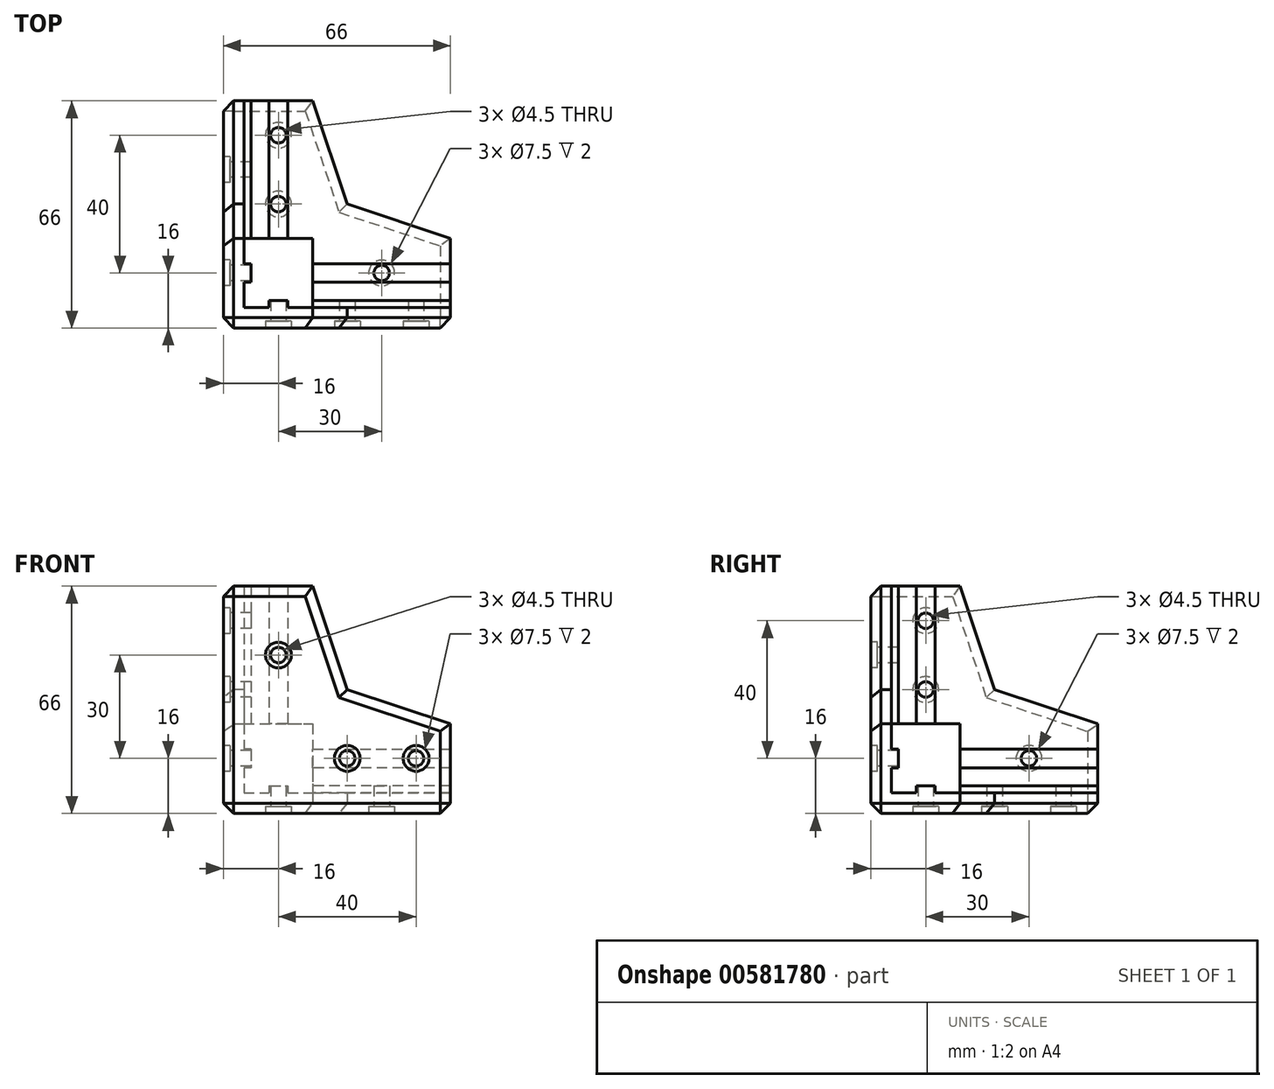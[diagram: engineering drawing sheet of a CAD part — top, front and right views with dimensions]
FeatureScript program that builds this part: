
annotation { "Feature Type Name" : "Feature", "Feature Type Description" : "" }
export const myFeature = defineFeature(function(context is Context, id is Id, definition is map)
    precondition{}
    {
        {
            var Q0;
            Q0=qCreatedBy(makeId("Top.planeOp"),FACE);
            var sketch = newSketch(context, id + "F0", { "sketchPlane" : qUnion([Q0])});
            skLineSegment(sketch, "E0", {"start": v(0, 0) * mm, "end": v(0, 66) * mm});
            skLineSegment(sketch, "E1", {"start": v(0, 66) * mm, "end": v(26, 66) * mm});
            skLineSegment(sketch, "E2", {"start": v(26, 66) * mm, "end": v(26, 26) * mm});
            skLineSegment(sketch, "E3", {"start": v(26, 26) * mm, "end": v(66, 26) * mm});
            skLineSegment(sketch, "E4", {"start": v(66, 26) * mm, "end": v(66, 0) * mm});
            skLineSegment(sketch, "E5", {"start": v(66, 0) * mm, "end": v(0, 0) * mm});
            skLineSegment(sketch, "E6", {"start": v(66, 6) * mm, "end": v(6, 6) * mm, "construction": true});
            skLineSegment(sketch, "E7", {"start": v(6, 6) * mm, "end": v(6, 66) * mm, "construction": true});
            skSolve(sketch);
        }
        {
            var Q0;
            Q0=qSketchRegion(id+"F0",true);
            extrude(context, id + "F1", {"entities" : qUnion([Q0]), "depth" : 6 * mm});
        }
        {
            var Q0;
            Q0=makeQuery(id+"F1.opExtrude","CAP_FACE",FACE,{"disambiguationData":[OSD([sQuery(id+"F0.wireOp",EDGE,"E0"),sQuery(id+"F0.wireOp",EDGE,"E1"),sQuery(id+"F0.wireOp",EDGE,"E2"),sQuery(id+"F0.wireOp",EDGE,"E3"),sQuery(id+"F0.wireOp",EDGE,"E4"),sQuery(id+"F0.wireOp",EDGE,"E5")])],"isStart":false});
            var sketch = newSketch(context, id + "F2", { "sketchPlane" : qUnion([Q0])});
            skLineSegment(sketch, "E8", {"start": v(0, 66) * mm, "end": v(6, 66) * mm});
            skLineSegment(sketch, "E9", {"start": v(6, 66) * mm, "end": v(6, 6) * mm});
            skLineSegment(sketch, "E10", {"start": v(6, 6) * mm, "end": v(66, 6) * mm});
            skLineSegment(sketch, "E11", {"start": v(66, 6) * mm, "end": v(66, 0) * mm});
            skLineSegment(sketch, "E12", {"start": v(66, 0) * mm, "end": v(0, 0) * mm});
            skLineSegment(sketch, "E13", {"start": v(0, 0) * mm, "end": v(0, 66) * mm});
            skSolve(sketch);
        }
        {
            var Q0;
            Q0=makeQuery(id+"F2.imprint","IMPRINT",FACE,{"disambiguationData":[TD([[makeQuery(id+"F2.imprint","IMPRINT",EDGE,{"derivedFrom":sQuery(id+"F2.wireOp",EDGE,"E8")}),-1.0]])]});
            extrude(context, id + "F3", {"entities" : qUnion([Q0]), "operationType" : NewBodyOperationType.ADD, "depth" : 20 * mm});
        }
        {
            var Q0;
            Q0=makeQuery(id+"F3.opExtrude","CAP_FACE",FACE,{"disambiguationData":[OSD([sQuery(id+"F2.wireOp",EDGE,"E8"),sQuery(id+"F2.wireOp",EDGE,"E9"),sQuery(id+"F2.wireOp",EDGE,"E10"),sQuery(id+"F2.wireOp",EDGE,"E11"),sQuery(id+"F2.wireOp",EDGE,"E12"),sQuery(id+"F2.wireOp",EDGE,"E13")])],"isStart":false});
            var sketch = newSketch(context, id + "F4", { "sketchPlane" : qUnion([Q0])});
            skLineSegment(sketch, "E14", {"start": v(6, 26) * mm, "end": v(0, 26) * mm});
            skLineSegment(sketch, "E15", {"start": v(0, 26) * mm, "end": v(0, 0) * mm});
            skLineSegment(sketch, "E16", {"start": v(0, 0) * mm, "end": v(26, 0) * mm});
            skLineSegment(sketch, "E17", {"start": v(26, 0) * mm, "end": v(26, 6) * mm});
            skLineSegment(sketch, "E18", {"start": v(26, 6) * mm, "end": v(6, 6) * mm});
            skLineSegment(sketch, "E19", {"start": v(6, 6) * mm, "end": v(6, 26) * mm});
            skSolve(sketch);
        }
        {
            var Q0;
            Q0=qSketchRegion(id+"F4",true);
            extrude(context, id + "F5", {"entities" : qUnion([Q0]), "operationType" : NewBodyOperationType.ADD, "depth" : 40 * mm});
        }
        {
            var Q0;
            Q0=makeQuery(id+"F1.opExtrude","CAP_FACE",FACE,{"disambiguationData":[OSD([sQuery(id+"F0.wireOp",EDGE,"E0"),sQuery(id+"F0.wireOp",EDGE,"E1"),sQuery(id+"F0.wireOp",EDGE,"E2"),sQuery(id+"F0.wireOp",EDGE,"E3"),sQuery(id+"F0.wireOp",EDGE,"E4"),sQuery(id+"F0.wireOp",EDGE,"E5")])],"isStart":false});
            var sketch = newSketch(context, id + "F6", { "sketchPlane" : qUnion([Q0])});
            skLineSegment(sketch, "E20", {"start": v(66, 16) * mm, "end": v(6, 16) * mm, "construction": true});
            skLineSegment(sketch, "E21", {"start": v(16, 66) * mm, "end": v(16, 6) * mm, "construction": true});
            skLineSegment(sketch, "E22", {"start": v(16, 6) * mm, "end": v(18.71, 6) * mm});
            skLineSegment(sketch, "E23", {"start": v(18.71, 6) * mm, "end": v(18.71, 8) * mm});
            skLineSegment(sketch, "E24", {"start": v(18.71, 8) * mm, "end": v(13.3, 8) * mm});
            skLineSegment(sketch, "E25", {"start": v(13.3, 8) * mm, "end": v(13.3, 6) * mm});
            skLineSegment(sketch, "E26", {"start": v(13.3, 6) * mm, "end": v(16, 6) * mm});
            skLineSegment(sketch, "E27", {"start": v(6, 16) * mm, "end": v(6, 18.7) * mm});
            skLineSegment(sketch, "E28", {"start": v(6, 18.7) * mm, "end": v(8, 18.7) * mm});
            skLineSegment(sketch, "E29", {"start": v(8, 18.7) * mm, "end": v(8, 13.29) * mm});
            skLineSegment(sketch, "E30", {"start": v(8, 13.29) * mm, "end": v(6, 13.29) * mm});
            skLineSegment(sketch, "E31", {"start": v(6, 13.29) * mm, "end": v(6, 16) * mm});
            skSolve(sketch);
        }
        {
            var Q0;
            Q0=qSketchRegion(id+"F6",true);
            extrude(context, id + "F7", {"entities" : qUnion([Q0]), "operationType" : NewBodyOperationType.ADD, "depth" : 60 * mm});
        }
        {
            var Q0;
            Q0=makeQuery(id+"F1.opExtrude","CAP_FACE",FACE,{"disambiguationData":[OSD([sQuery(id+"F0.wireOp",EDGE,"E0"),sQuery(id+"F0.wireOp",EDGE,"E1"),sQuery(id+"F0.wireOp",EDGE,"E2"),sQuery(id+"F0.wireOp",EDGE,"E3"),sQuery(id+"F0.wireOp",EDGE,"E4"),sQuery(id+"F0.wireOp",EDGE,"E5")])],"isStart":false});
            var sketch = newSketch(context, id + "F8", { "sketchPlane" : qUnion([Q0])});
            skLineSegment(sketch, "E32", {"start": v(66, 16) * mm, "end": v(8, 16) * mm, "construction": true});
            skLineSegment(sketch, "E33", {"start": v(66, 16) * mm, "end": v(66, 18.7) * mm});
            skLineSegment(sketch, "E34", {"start": v(66, 18.7) * mm, "end": v(26, 18.7) * mm});
            skLineSegment(sketch, "E35", {"start": v(26, 18.7) * mm, "end": v(26, 13.29) * mm});
            skLineSegment(sketch, "E36", {"start": v(26, 13.29) * mm, "end": v(66, 13.29) * mm});
            skLineSegment(sketch, "E37", {"start": v(66, 13.29) * mm, "end": v(66, 16) * mm});
            skLineSegment(sketch, "E38", {"start": v(16, 66) * mm, "end": v(16, 8) * mm, "construction": true});
            skLineSegment(sketch, "E39", {"start": v(16, 66) * mm, "end": v(13.3, 66) * mm});
            skLineSegment(sketch, "E40", {"start": v(13.3, 66) * mm, "end": v(13.3, 26) * mm});
            skLineSegment(sketch, "E41", {"start": v(13.3, 26) * mm, "end": v(18.7, 26) * mm});
            skLineSegment(sketch, "E42", {"start": v(18.7, 26) * mm, "end": v(18.7, 66) * mm});
            skLineSegment(sketch, "E43", {"start": v(18.7, 66) * mm, "end": v(16, 66) * mm});
            skSolve(sketch);
        }
        {
            var Q0;
            Q0=qSketchRegion(id+"F8",true);
            extrude(context, id + "F9", {"entities" : qUnion([Q0]), "operationType" : NewBodyOperationType.ADD, "depth" : 2 * mm});
        }
        {
            var Q0;
            {var subQ1=sQuery(id+"F2.wireOp",EDGE,"E10");var subQ2=sQuery(id+"F0.wireOp",EDGE,"E4");var subQ3=sQuery(id+"F4.wireOp",EDGE,"E18");Q0=makeQuery(id+"F7.boolean.opBoolean","SPLIT",FACE,{"disambiguationData":[TD([makeQuery(id+"F1.opExtrude","SWEPT_FACE",FACE,{"disambiguationData":[OSD([subQ2])]})])],"derivedFrom":makeQuery(id+"F5.boolean.opBoolean","MERGE",FACE,{"derivedFrom":[makeQuery(id+"F3.opExtrude","SWEPT_FACE",FACE,{"disambiguationData":[OSD([subQ1])]}),makeQuery(id+"F5.opExtrude","SWEPT_FACE",FACE,{"disambiguationData":[OSD([subQ3])]})]})});}
            var sketch = newSketch(context, id + "F10", { "sketchPlane" : qUnion([Q0])});
            skLineSegment(sketch, "E44", {"start": v(-66, 16) * mm, "end": v(-26, 16) * mm, "construction": true});
            skLineSegment(sketch, "E45", {"start": v(-66, 16) * mm, "end": v(-66, 13.3) * mm});
            skLineSegment(sketch, "E46", {"start": v(-66, 13.3) * mm, "end": v(-26, 13.3) * mm});
            skLineSegment(sketch, "E47", {"start": v(-26, 13.3) * mm, "end": v(-26, 16) * mm});
            skLineSegment(sketch, "E48", {"start": v(-26, 18.71) * mm, "end": v(-66, 18.71) * mm});
            skLineSegment(sketch, "E49", {"start": v(-66, 18.71) * mm, "end": v(-66, 16) * mm});
            skLineSegment(sketch, "E50", {"start": v(-26, 18.71) * mm, "end": v(-26, 16) * mm});
            skSolve(sketch);
        }
        {
            var Q0;
            Q0=qSketchRegion(id+"F10",true);
            extrude(context, id + "F11", {"entities" : qUnion([Q0]), "operationType" : NewBodyOperationType.ADD, "depth" : 2 * mm});
        }
        {
            var Q0;
            {var subQ0=sQuery(id+"F2.wireOp",EDGE,"E9");var subQ3=sQuery(id+"F0.wireOp",EDGE,"E1");var subQ5=sQuery(id+"F4.wireOp",EDGE,"E19");Q0=makeQuery(id+"F7.boolean.opBoolean","SPLIT",FACE,{"disambiguationData":[TD([makeQuery(id+"F1.opExtrude","SWEPT_FACE",FACE,{"disambiguationData":[OSD([subQ3])]})])],"derivedFrom":makeQuery(id+"F5.boolean.opBoolean","MERGE",FACE,{"derivedFrom":[makeQuery(id+"F3.opExtrude","SWEPT_FACE",FACE,{"disambiguationData":[OSD([subQ0])]}),makeQuery(id+"F5.opExtrude","SWEPT_FACE",FACE,{"disambiguationData":[OSD([subQ5])]})]})});}
            var sketch = newSketch(context, id + "F12", { "sketchPlane" : qUnion([Q0])});
            skLineSegment(sketch, "E51", {"start": v(66, 16) * mm, "end": v(26, 16) * mm, "construction": true});
            skLineSegment(sketch, "E52", {"start": v(66, 16) * mm, "end": v(66, 18.71) * mm});
            skLineSegment(sketch, "E53", {"start": v(66, 18.71) * mm, "end": v(26, 18.7) * mm});
            skLineSegment(sketch, "E54", {"start": v(26, 18.7) * mm, "end": v(26, 13.29) * mm});
            skLineSegment(sketch, "E55", {"start": v(26, 13.29) * mm, "end": v(66, 13.29) * mm});
            skLineSegment(sketch, "E56", {"start": v(66, 16) * mm, "end": v(66, 13.29) * mm});
            skSolve(sketch);
        }
        {
            var Q0;
            Q0=qSketchRegion(id+"F12",true);
            extrude(context, id + "F13", {"entities" : qUnion([Q0]), "operationType" : NewBodyOperationType.ADD, "depth" : 2 * mm});
        }
        {
            var Q0;
            Q0=makeQuery(id+"F5.boolean.opBoolean","MERGE",FACE,{"derivedFrom":[makeQuery(id+"F3.boolean.opBoolean","MERGE",FACE,{"derivedFrom":[makeQuery(id+"F1.opExtrude","SWEPT_FACE",FACE,{"disambiguationData":[OSD([sQuery(id+"F0.wireOp",EDGE,"E5")])]}),makeQuery(id+"F3.opExtrude","SWEPT_FACE",FACE,{"disambiguationData":[OSD([sQuery(id+"F2.wireOp",EDGE,"E12")])]})]}),makeQuery(id+"F5.opExtrude","SWEPT_FACE",FACE,{"disambiguationData":[OSD([sQuery(id+"F4.wireOp",EDGE,"E16")])]})]});
            var sketch = newSketch(context, id + "F14", { "sketchPlane" : qUnion([Q0])});
            skLineSegment(sketch, "E57", {"start": v(6, 66) * mm, "end": v(6, 6) * mm, "construction": true});
            skLineSegment(sketch, "E58", {"start": v(6, 6) * mm, "end": v(66, 6) * mm, "construction": true});
            skCircle(sketch, "E59", {"center": v(56, 16) * mm, "radius": 2.25 * mm});
            skCircle(sketch, "E60", {"center": v(36, 16) * mm, "radius": 2.25 * mm});
            skCircle(sketch, "E61", {"center": v(16, 46) * mm, "radius": 2.25 * mm});
            skLineSegment(sketch, "E62", {"start": v(26, 26) * mm, "end": v(6, 26) * mm, "construction": true});
            skLineSegment(sketch, "E63", {"start": v(26, 26) * mm, "end": v(26, 6) * mm, "construction": true});
            skSolve(sketch);
        }
        {
            var Q0;
            Q0=makeQuery(id+"F14.imprint","IMPRINT",FACE,{"disambiguationData":[TD([[makeQuery(id+"F14.imprint","IMPRINT",EDGE,{"derivedFrom":sQuery(id+"F14.wireOp",EDGE,"E59")}),1.0]])]});
            var Q1;
            Q1=makeQuery(id+"F14.imprint","IMPRINT",FACE,{"disambiguationData":[TD([[makeQuery(id+"F14.imprint","IMPRINT",EDGE,{"derivedFrom":sQuery(id+"F14.wireOp",EDGE,"E61")}),1.0]])]});
            var Q2;
            Q2=makeQuery(id+"F14.imprint","IMPRINT",FACE,{"disambiguationData":[TD([[makeQuery(id+"F14.imprint","IMPRINT",EDGE,{"derivedFrom":sQuery(id+"F14.wireOp",EDGE,"E60")}),1.0]])]});
            extrude(context, id + "F15", {"entities" : qUnion([Q0, Q1, Q2]), "operationType" : NewBodyOperationType.REMOVE, "endBound" : BoundingType.UP_TO_NEXT, "oppositeDirection" : true, "depth" : 25 * mm});
        }
        {
            var Q0;
            Q0=makeQuery(id+"F5.boolean.opBoolean","MERGE",FACE,{"derivedFrom":[makeQuery(id+"F3.boolean.opBoolean","MERGE",FACE,{"derivedFrom":[makeQuery(id+"F1.opExtrude","SWEPT_FACE",FACE,{"disambiguationData":[OSD([sQuery(id+"F0.wireOp",EDGE,"E0")])]}),makeQuery(id+"F3.opExtrude","SWEPT_FACE",FACE,{"disambiguationData":[OSD([sQuery(id+"F2.wireOp",EDGE,"E13")])]})]}),makeQuery(id+"F5.opExtrude","SWEPT_FACE",FACE,{"disambiguationData":[OSD([sQuery(id+"F4.wireOp",EDGE,"E15")])]})]});
            var sketch = newSketch(context, id + "F16", { "sketchPlane" : qUnion([Q0])});
            skLineSegment(sketch, "E64", {"start": v(-6, 66) * mm, "end": v(-6, 6) * mm, "construction": true});
            skLineSegment(sketch, "E65", {"start": v(-6, 6) * mm, "end": v(-66, 6) * mm, "construction": true});
            skCircle(sketch, "E66", {"center": v(-16, 56) * mm, "radius": 2.25 * mm});
            skCircle(sketch, "E67", {"center": v(-46, 16) * mm, "radius": 2.25 * mm});
            skCircle(sketch, "E68", {"center": v(-16, 36) * mm, "radius": 2.25 * mm});
            skSolve(sketch);
        }
        {
            var Q0;
            Q0=qSketchRegion(id+"F16",true);
            extrude(context, id + "F17", {"entities" : qUnion([Q0]), "operationType" : NewBodyOperationType.REMOVE, "endBound" : BoundingType.UP_TO_NEXT, "oppositeDirection" : true, "depth" : 25 * mm});
        }
        {
            var Q0;
            Q0=makeQuery(id+"F1.opExtrude","CAP_FACE",FACE,{"disambiguationData":[OSD([sQuery(id+"F0.wireOp",EDGE,"E0"),sQuery(id+"F0.wireOp",EDGE,"E1"),sQuery(id+"F0.wireOp",EDGE,"E2"),sQuery(id+"F0.wireOp",EDGE,"E3"),sQuery(id+"F0.wireOp",EDGE,"E4"),sQuery(id+"F0.wireOp",EDGE,"E5")])],"isStart":true});
            var sketch = newSketch(context, id + "F18", { "sketchPlane" : qUnion([Q0])});
            skLineSegment(sketch, "E69", {"start": v(66, -6) * mm, "end": v(6, -6) * mm, "construction": true});
            skLineSegment(sketch, "E70", {"start": v(6, -6) * mm, "end": v(6, -66) * mm, "construction": true});
            skCircle(sketch, "E71", {"center": v(46, -16) * mm, "radius": 2.25 * mm});
            skCircle(sketch, "E72", {"center": v(16, -56) * mm, "radius": 2.25 * mm});
            skCircle(sketch, "E73", {"center": v(16, -36) * mm, "radius": 2.25 * mm});
            skSolve(sketch);
        }
        {
            var Q0;
            Q0=qSketchRegion(id+"F18",true);
            extrude(context, id + "F19", {"entities" : qUnion([Q0]), "operationType" : NewBodyOperationType.REMOVE, "endBound" : BoundingType.UP_TO_NEXT, "oppositeDirection" : true, "depth" : 25 * mm});
        }
        {
            var Q0;
            Q0=makeQuery(id+"F5.boolean.opBoolean","MERGE",FACE,{"derivedFrom":[makeQuery(id+"F3.boolean.opBoolean","MERGE",FACE,{"derivedFrom":[makeQuery(id+"F1.opExtrude","SWEPT_FACE",FACE,{"disambiguationData":[OSD([sQuery(id+"F0.wireOp",EDGE,"E5")])]}),makeQuery(id+"F3.opExtrude","SWEPT_FACE",FACE,{"disambiguationData":[OSD([sQuery(id+"F2.wireOp",EDGE,"E12")])]})]}),makeQuery(id+"F5.opExtrude","SWEPT_FACE",FACE,{"disambiguationData":[OSD([sQuery(id+"F4.wireOp",EDGE,"E16")])]})]});
            var sketch = newSketch(context, id + "F20", { "sketchPlane" : qUnion([Q0])});
            skCircle(sketch, "E74", {"center": v(16, 46) * mm, "radius": 3.75 * mm});
            skCircle(sketch, "E75", {"center": v(36, 16) * mm, "radius": 3.75 * mm});
            skCircle(sketch, "E76", {"center": v(56, 16) * mm, "radius": 3.75 * mm});
            skSolve(sketch);
        }
        {
            var Q0;
            Q0=qSketchRegion(id+"F20",true);
            extrude(context, id + "F21", {"entities" : qUnion([Q0]), "operationType" : NewBodyOperationType.REMOVE, "oppositeDirection" : true, "depth" : 2 * mm});
        }
        {
            var Q0;
            Q0=makeQuery(id+"F5.boolean.opBoolean","MERGE",FACE,{"derivedFrom":[makeQuery(id+"F3.boolean.opBoolean","MERGE",FACE,{"derivedFrom":[makeQuery(id+"F1.opExtrude","SWEPT_FACE",FACE,{"disambiguationData":[OSD([sQuery(id+"F0.wireOp",EDGE,"E0")])]}),makeQuery(id+"F3.opExtrude","SWEPT_FACE",FACE,{"disambiguationData":[OSD([sQuery(id+"F2.wireOp",EDGE,"E13")])]})]}),makeQuery(id+"F5.opExtrude","SWEPT_FACE",FACE,{"disambiguationData":[OSD([sQuery(id+"F4.wireOp",EDGE,"E15")])]})]});
            var sketch = newSketch(context, id + "F22", { "sketchPlane" : qUnion([Q0])});
            skCircle(sketch, "E77", {"center": v(-16, 56) * mm, "radius": 3.75 * mm});
            skCircle(sketch, "E78", {"center": v(-46, 16) * mm, "radius": 3.75 * mm});
            skCircle(sketch, "E79", {"center": v(-16, 36) * mm, "radius": 3.75 * mm});
            skSolve(sketch);
        }
        {
            var Q0;
            Q0=qSketchRegion(id+"F22",true);
            extrude(context, id + "F23", {"entities" : qUnion([Q0]), "operationType" : NewBodyOperationType.REMOVE, "oppositeDirection" : true, "depth" : 2 * mm});
        }
        {
            var Q0;
            Q0=makeQuery(id+"F1.opExtrude","CAP_FACE",FACE,{"disambiguationData":[OSD([sQuery(id+"F0.wireOp",EDGE,"E0"),sQuery(id+"F0.wireOp",EDGE,"E1"),sQuery(id+"F0.wireOp",EDGE,"E2"),sQuery(id+"F0.wireOp",EDGE,"E3"),sQuery(id+"F0.wireOp",EDGE,"E4"),sQuery(id+"F0.wireOp",EDGE,"E5")])],"isStart":true});
            var sketch = newSketch(context, id + "F24", { "sketchPlane" : qUnion([Q0])});
            skCircle(sketch, "E80", {"center": v(16, -56) * mm, "radius": 3.75 * mm});
            skCircle(sketch, "E81", {"center": v(46, -16) * mm, "radius": 3.75 * mm});
            skCircle(sketch, "E82", {"center": v(16, -36) * mm, "radius": 3.75 * mm});
            skSolve(sketch);
        }
        {
            var Q0;
            Q0=qSketchRegion(id+"F24",true);
            extrude(context, id + "F25", {"entities" : qUnion([Q0]), "operationType" : NewBodyOperationType.REMOVE, "oppositeDirection" : true, "depth" : 2 * mm});
        }
        {
            var Q0;
            Q0=makeQuery(id+"F1.opExtrude","CAP_FACE",FACE,{"disambiguationData":[OSD([sQuery(id+"F0.wireOp",EDGE,"E0"),sQuery(id+"F0.wireOp",EDGE,"E1"),sQuery(id+"F0.wireOp",EDGE,"E2"),sQuery(id+"F0.wireOp",EDGE,"E3"),sQuery(id+"F0.wireOp",EDGE,"E4"),sQuery(id+"F0.wireOp",EDGE,"E5")])],"isStart":false});
            var sketch = newSketch(context, id + "F26", { "sketchPlane" : qUnion([Q0])});
            skLineSegment(sketch, "E83.bottom", {"start": v(6, 6) * mm, "end": v(26, 6) * mm});
            skLineSegment(sketch, "E83.top", {"start": v(6, 26) * mm, "end": v(26, 26) * mm});
            skLineSegment(sketch, "E83.left", {"start": v(6, 6) * mm, "end": v(6, 26) * mm});
            skLineSegment(sketch, "E83.right", {"start": v(26, 6) * mm, "end": v(26, 26) * mm});
            skSolve(sketch);
        }
        {
            var Q0;
            Q0=qSketchRegion(id+"F26",true);
            extrude(context, id + "F27", {"entities" : qUnion([Q0]), "operationType" : NewBodyOperationType.ADD, "depth" : 20 * mm});
        }
        {
            var Q0;
            Q0=makeQuery(id+"F5.boolean.opBoolean","MERGE",FACE,{"derivedFrom":[makeQuery(id+"F3.boolean.opBoolean","MERGE",FACE,{"derivedFrom":[makeQuery(id+"F1.opExtrude","SWEPT_FACE",FACE,{"disambiguationData":[OSD([sQuery(id+"F0.wireOp",EDGE,"E5")])]}),makeQuery(id+"F3.opExtrude","SWEPT_FACE",FACE,{"disambiguationData":[OSD([sQuery(id+"F2.wireOp",EDGE,"E12")])]})]}),makeQuery(id+"F5.opExtrude","SWEPT_FACE",FACE,{"disambiguationData":[OSD([sQuery(id+"F4.wireOp",EDGE,"E16")])]})]});
            var sketch = newSketch(context, id + "F28", { "sketchPlane" : qUnion([Q0])});
            skLineSegment(sketch, "E84", {"start": v(26, 36) * mm, "end": v(36, 36) * mm, "construction": true});
            skLineSegment(sketch, "E85", {"start": v(36, 36) * mm, "end": v(36, 26) * mm, "construction": true});
            skLineSegment(sketch, "E86", {"start": v(26, 66) * mm, "end": v(36, 36) * mm});
            skLineSegment(sketch, "E87", {"start": v(36, 36) * mm, "end": v(66, 26) * mm});
            skLineSegment(sketch, "E88", {"start": v(66, 26) * mm, "end": v(26, 26) * mm});
            skLineSegment(sketch, "E89", {"start": v(26, 26) * mm, "end": v(26, 66) * mm});
            skSolve(sketch);
        }
        {
            var Q0;
            Q0=qSketchRegion(id+"F28",true);
            extrude(context, id + "F29", {"entities" : qUnion([Q0]), "operationType" : NewBodyOperationType.ADD, "oppositeDirection" : true, "depth" : 6 * mm});
        }
        {
            var Q0;
            Q0=makeQuery(id+"F5.boolean.opBoolean","MERGE",FACE,{"derivedFrom":[makeQuery(id+"F3.boolean.opBoolean","MERGE",FACE,{"derivedFrom":[makeQuery(id+"F1.opExtrude","SWEPT_FACE",FACE,{"disambiguationData":[OSD([sQuery(id+"F0.wireOp",EDGE,"E0")])]}),makeQuery(id+"F3.opExtrude","SWEPT_FACE",FACE,{"disambiguationData":[OSD([sQuery(id+"F2.wireOp",EDGE,"E13")])]})]}),makeQuery(id+"F5.opExtrude","SWEPT_FACE",FACE,{"disambiguationData":[OSD([sQuery(id+"F4.wireOp",EDGE,"E15")])]})]});
            var sketch = newSketch(context, id + "F30", { "sketchPlane" : qUnion([Q0])});
            skLineSegment(sketch, "E90", {"start": v(-26, 36) * mm, "end": v(-36, 36) * mm, "construction": true});
            skLineSegment(sketch, "E91", {"start": v(-36, 36) * mm, "end": v(-36, 26) * mm, "construction": true});
            skLineSegment(sketch, "E92", {"start": v(-26, 66) * mm, "end": v(-36, 36) * mm});
            skLineSegment(sketch, "E93", {"start": v(-36, 36) * mm, "end": v(-66, 26) * mm});
            skLineSegment(sketch, "E94", {"start": v(-66, 26) * mm, "end": v(-26, 26) * mm});
            skLineSegment(sketch, "E95", {"start": v(-26, 26) * mm, "end": v(-26, 66) * mm});
            skSolve(sketch);
        }
        {
            var Q0;
            Q0=qSketchRegion(id+"F30",true);
            extrude(context, id + "F31", {"entities" : qUnion([Q0]), "operationType" : NewBodyOperationType.ADD, "oppositeDirection" : true, "depth" : 6 * mm});
        }
        {
            var Q0;
            Q0=makeQuery(id+"F1.opExtrude","CAP_FACE",FACE,{"disambiguationData":[OSD([sQuery(id+"F0.wireOp",EDGE,"E0"),sQuery(id+"F0.wireOp",EDGE,"E1"),sQuery(id+"F0.wireOp",EDGE,"E2"),sQuery(id+"F0.wireOp",EDGE,"E3"),sQuery(id+"F0.wireOp",EDGE,"E4"),sQuery(id+"F0.wireOp",EDGE,"E5")])],"isStart":true});
            var sketch = newSketch(context, id + "F32", { "sketchPlane" : qUnion([Q0])});
            skLineSegment(sketch, "E96", {"start": v(36, -26) * mm, "end": v(36, -36) * mm, "construction": true});
            skLineSegment(sketch, "E97", {"start": v(36, -36) * mm, "end": v(26, -36) * mm, "construction": true});
            skLineSegment(sketch, "E98", {"start": v(66, -26) * mm, "end": v(36, -36) * mm});
            skLineSegment(sketch, "E99", {"start": v(36, -36) * mm, "end": v(26, -66) * mm});
            skLineSegment(sketch, "E100", {"start": v(26, -66) * mm, "end": v(26, -26) * mm});
            skLineSegment(sketch, "E101", {"start": v(26, -26) * mm, "end": v(66, -26) * mm});
            skSolve(sketch);
        }
        {
            var Q0;
            Q0=qSketchRegion(id+"F32",true);
            extrude(context, id + "F33", {"entities" : qUnion([Q0]), "operationType" : NewBodyOperationType.ADD, "oppositeDirection" : true, "depth" : 6 * mm});
        }
        {
            var Q0;
            Q0=makeQuery(id+"F1.opExtrude","CAP_EDGE",EDGE,{"disambiguationData":[OSD([sQuery(id+"F0.wireOp",EDGE,"E5")])],"isStart":true});
            var Q1;
            Q1=makeQuery(id+"F1.opExtrude","CAP_EDGE",EDGE,{"disambiguationData":[OSD([sQuery(id+"F0.wireOp",EDGE,"E4")])],"isStart":true});
            var Q2;
            Q2=makeQuery(id+"F33.opExtrude","CAP_EDGE",EDGE,{"disambiguationData":[OSD([sQuery(id+"F32.wireOp",EDGE,"E98")])],"isStart":true});
            var Q3;
            Q3=makeQuery(id+"F33.opExtrude","CAP_EDGE",EDGE,{"disambiguationData":[OSD([sQuery(id+"F32.wireOp",EDGE,"E99")])],"isStart":true});
            var Q4;
            Q4=makeQuery(id+"F1.opExtrude","CAP_EDGE",EDGE,{"disambiguationData":[OSD([sQuery(id+"F0.wireOp",EDGE,"E1")])],"isStart":true});
            var Q5;
            Q5=makeQuery(id+"F1.opExtrude","CAP_EDGE",EDGE,{"disambiguationData":[OSD([sQuery(id+"F0.wireOp",EDGE,"E0")])],"isStart":true});
            var Q6;
            Q6=makeQuery(id+"F3.boolean.opBoolean","MERGE",EDGE,{"derivedFrom":[makeQuery(id+"F1.opExtrude","SWEPT_EDGE",EDGE,{"disambiguationData":[OSD([sQuery(id+"F0.wireOp",EDGE,"E0"),sQuery(id+"F0.wireOp",EDGE,"E1")])]}),makeQuery(id+"F3.opExtrude","SWEPT_EDGE",EDGE,{"disambiguationData":[OSD([sQuery(id+"F2.wireOp",EDGE,"E8"),sQuery(id+"F2.wireOp",EDGE,"E13")])]})]});
            var Q7;
            Q7=makeQuery(id+"F31.opExtrude","CAP_EDGE",EDGE,{"disambiguationData":[OSD([sQuery(id+"F30.wireOp",EDGE,"E93")])],"isStart":true});
            var Q8;
            Q8=makeQuery(id+"F31.opExtrude","CAP_EDGE",EDGE,{"disambiguationData":[OSD([sQuery(id+"F30.wireOp",EDGE,"E92")])],"isStart":true});
            var Q9;
            Q9=makeQuery(id+"F5.opExtrude","CAP_EDGE",EDGE,{"disambiguationData":[OSD([sQuery(id+"F4.wireOp",EDGE,"E15")])],"isStart":false});
            var Q10;
            Q10=makeQuery(id+"F5.boolean.opBoolean","MERGE",EDGE,{"derivedFrom":[makeQuery(id+"F3.boolean.opBoolean","MERGE",EDGE,{"derivedFrom":[makeQuery(id+"F1.opExtrude","SWEPT_EDGE",EDGE,{"disambiguationData":[OSD([sQuery(id+"F0.wireOp",EDGE,"E0"),sQuery(id+"F0.wireOp",EDGE,"E5")])]}),makeQuery(id+"F3.opExtrude","SWEPT_EDGE",EDGE,{"disambiguationData":[OSD([sQuery(id+"F2.wireOp",EDGE,"E12"),sQuery(id+"F2.wireOp",EDGE,"E13")])]})]}),makeQuery(id+"F5.opExtrude","SWEPT_EDGE",EDGE,{"disambiguationData":[OSD([sQuery(id+"F4.wireOp",EDGE,"E15"),sQuery(id+"F4.wireOp",EDGE,"E16")])]})]});
            var Q11;
            Q11=makeQuery(id+"F3.boolean.opBoolean","MERGE",EDGE,{"derivedFrom":[makeQuery(id+"F1.opExtrude","SWEPT_EDGE",EDGE,{"disambiguationData":[OSD([sQuery(id+"F0.wireOp",EDGE,"E4"),sQuery(id+"F0.wireOp",EDGE,"E5")])]}),makeQuery(id+"F3.opExtrude","SWEPT_EDGE",EDGE,{"disambiguationData":[OSD([sQuery(id+"F2.wireOp",EDGE,"E11"),sQuery(id+"F2.wireOp",EDGE,"E12")])]})]});
            var Q12;
            Q12=makeQuery(id+"F29.opExtrude","CAP_EDGE",EDGE,{"disambiguationData":[OSD([sQuery(id+"F28.wireOp",EDGE,"E87")])],"isStart":true});
            var Q13;
            Q13=makeQuery(id+"F29.opExtrude","CAP_EDGE",EDGE,{"disambiguationData":[OSD([sQuery(id+"F28.wireOp",EDGE,"E86")])],"isStart":true});
            var Q14;
            Q14=makeQuery(id+"F5.opExtrude","CAP_EDGE",EDGE,{"disambiguationData":[OSD([sQuery(id+"F4.wireOp",EDGE,"E16")])],"isStart":false});
            chamfer(context, id + "F34", {"entities" : qUnion([Q0, Q1, Q2, Q3, Q4, Q5, Q6, Q7, Q8, Q9, Q10, Q11, Q12, Q13, Q14]), "width" : 3 * mm, "tangentPropagation" : true});
        }
    });
